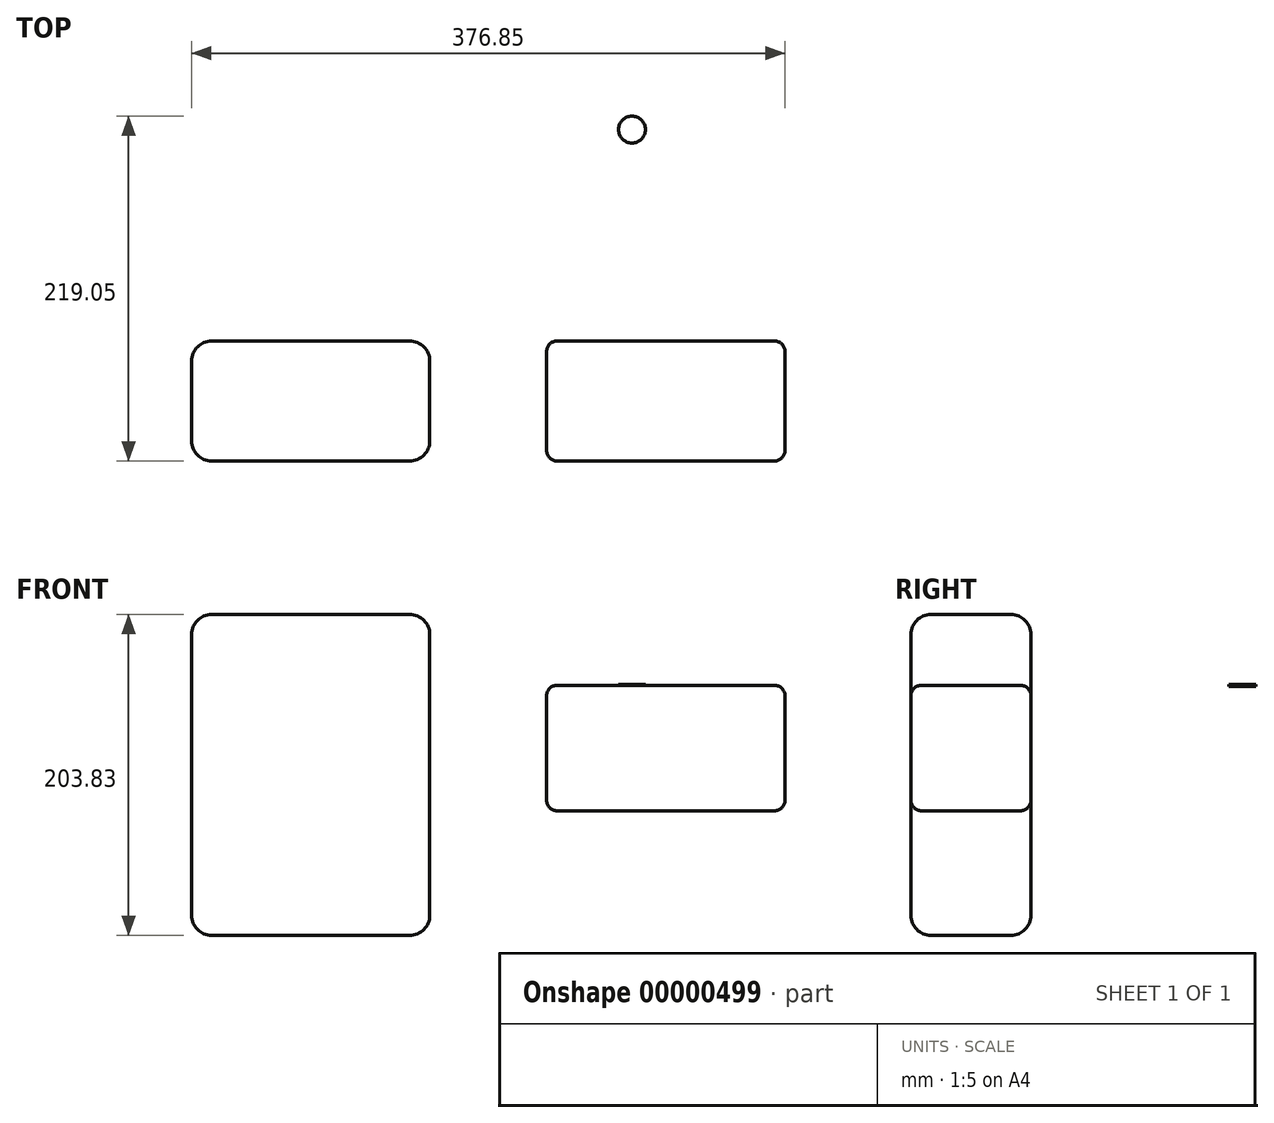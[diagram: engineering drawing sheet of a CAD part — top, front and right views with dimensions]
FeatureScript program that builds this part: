
annotation { "Feature Type Name" : "Feature", "Feature Type Description" : "" }
export const myFeature = defineFeature(function(context is Context, id is Id, definition is map)
    precondition{}
    {
        {
            var Q0;
            Q0=qCreatedBy(makeId("Front.planeOp"),FACE);
            var sketch = newSketch(context, id + "F0", { "sketchPlane" : qUnion([Q0])});
            skLineSegment(sketch, "E0.bottom", {"start": v(127.92, -65.75) * mm, "end": v(-23.48, -65.75) * mm});
            skLineSegment(sketch, "E0.top", {"start": v(127.92, 14) * mm, "end": v(-23.48, 14) * mm});
            skLineSegment(sketch, "E0.left", {"start": v(127.92, -65.75) * mm, "end": v(127.92, 14) * mm});
            skLineSegment(sketch, "E0.right", {"start": v(-23.48, -65.75) * mm, "end": v(-23.48, 14) * mm});
            skSolve(sketch);
        }
        {
            var Q0;
            Q0=makeQuery(id+"F0.imprint","IMPRINT",FACE,{"disambiguationData":[TD([[makeQuery(id+"F0.imprint","IMPRINT",EDGE,{"derivedFrom":sQuery(id+"F0.wireOp",EDGE,"E0.bottom")}),-1.0]])]});
            extrude(context, id + "F1", {"entities" : qUnion([Q0]), "depth" : 76.2 * mm});
        }
        {
            var Q0;
            Q0=qCreatedBy(makeId("Top.planeOp"),FACE);
            cPlane(context, id + "F2", {"entities" : qUnion([Q0]), "cplaneType" : CPlaneType.OFFSET, "offset" : 13.2 * mm, "width" : 152.4 * mm, "height" : 152.4 * mm});
        }
        {
            var Q0;
            Q0=qCreatedBy(id+"F2.planeOp",FACE);
            var sketch = newSketch(context, id + "F3", { "sketchPlane" : qUnion([Q0])});
            skCircle(sketch, "E1", {"center": v(30.72, 134.33) * mm, "radius": 8.53 * mm});
            skSolve(sketch);
        }
        {
            var Q0;
            Q0=makeQuery(id+"F3.imprint","IMPRINT",FACE,{"disambiguationData":[TD([[makeQuery(id+"F3.imprint","IMPRINT",EDGE,{"derivedFrom":sQuery(id+"F3.wireOp",EDGE,"E1")}),1.0]])]});
            extrude(context, id + "F4", {"entities" : qUnion([Q0]), "depth" : 1.27 * mm});
        }
        {
            var Q0;
            Q0=qCreatedBy(makeId("Front.planeOp"),FACE);
            var sketch = newSketch(context, id + "F5", { "sketchPlane" : qUnion([Q0])});
            skLineSegment(sketch, "E2.bottom", {"start": v(-97.7, 58.95) * mm, "end": v(-248.93, 58.95) * mm});
            skLineSegment(sketch, "E2.top", {"start": v(-97.7, -144.88) * mm, "end": v(-248.93, -144.88) * mm});
            skLineSegment(sketch, "E2.left", {"start": v(-97.7, 58.95) * mm, "end": v(-97.7, -144.88) * mm});
            skLineSegment(sketch, "E2.right", {"start": v(-248.93, 58.95) * mm, "end": v(-248.93, -144.88) * mm});
            skSolve(sketch);
        }
        {
            var Q0;
            Q0=makeQuery(id+"F5.imprint","IMPRINT",FACE,{"disambiguationData":[TD([[makeQuery(id+"F5.imprint","IMPRINT",EDGE,{"derivedFrom":sQuery(id+"F5.wireOp",EDGE,"E2.bottom")}),1.0]])]});
            extrude(context, id + "F6", {"entities" : qUnion([Q0]), "depth" : 76.2 * mm});
        }
        {
            var Q0;
            Q0=makeQuery(id+"F6.opExtrude","CAP_FACE",FACE,{"disambiguationData":[OSD([sQuery(id+"F5.wireOp",EDGE,"E2.bottom"),sQuery(id+"F5.wireOp",EDGE,"E2.top"),sQuery(id+"F5.wireOp",EDGE,"E2.left"),sQuery(id+"F5.wireOp",EDGE,"E2.right")])],"isStart":false});
            var Q1;
            Q1=makeQuery(id+"F6.opExtrude","SWEPT_FACE",FACE,{"disambiguationData":[OSD([sQuery(id+"F5.wireOp",EDGE,"E2.right")])]});
            var Q2;
            Q2=makeQuery(id+"F6.opExtrude","CAP_EDGE",EDGE,{"disambiguationData":[OSD([sQuery(id+"F5.wireOp",EDGE,"E2.bottom")])],"isStart":true});
            var Q3;
            Q3=makeQuery(id+"F6.opExtrude","SWEPT_FACE",FACE,{"disambiguationData":[OSD([sQuery(id+"F5.wireOp",EDGE,"E2.bottom")])]});
            var Q4;
            Q4=makeQuery(id+"F6.opExtrude","CAP_EDGE",EDGE,{"disambiguationData":[OSD([sQuery(id+"F5.wireOp",EDGE,"E2.left")])],"isStart":true});
            var Q5;
            Q5=makeQuery(id+"F6.opExtrude","CAP_FACE",FACE,{"disambiguationData":[OSD([sQuery(id+"F5.wireOp",EDGE,"E2.bottom"),sQuery(id+"F5.wireOp",EDGE,"E2.top"),sQuery(id+"F5.wireOp",EDGE,"E2.left"),sQuery(id+"F5.wireOp",EDGE,"E2.right")])],"isStart":true});
            var Q6;
            Q6=makeQuery(id+"F6.opExtrude","SWEPT_EDGE",EDGE,{"disambiguationData":[OSD([sQuery(id+"F5.wireOp",EDGE,"E2.top"),sQuery(id+"F5.wireOp",EDGE,"E2.left")])]});
            fillet(context, id + "F7", {"entities" : qUnion([Q0, Q1, Q2, Q3, Q4, Q5, Q6]), "radius" : 12.7 * mm, "tangentPropagation" : true, "allowEdgeOverflow" : false});
        }
        {
            var Q0;
            Q0=makeQuery(id+"F1.opExtrude","CAP_EDGE",EDGE,{"disambiguationData":[OSD([sQuery(id+"F0.wireOp",EDGE,"E0.right")])],"isStart":false});
            var Q1;
            Q1=makeQuery(id+"F1.opExtrude","CAP_EDGE",EDGE,{"disambiguationData":[OSD([sQuery(id+"F0.wireOp",EDGE,"E0.bottom")])],"isStart":false});
            var Q2;
            Q2=makeQuery(id+"F1.opExtrude","CAP_EDGE",EDGE,{"disambiguationData":[OSD([sQuery(id+"F0.wireOp",EDGE,"E0.left")])],"isStart":false});
            var Q3;
            Q3=makeQuery(id+"F1.opExtrude","SWEPT_EDGE",EDGE,{"disambiguationData":[OSD([sQuery(id+"F0.wireOp",EDGE,"E0.top"),sQuery(id+"F0.wireOp",EDGE,"E0.right")])]});
            var Q4;
            Q4=makeQuery(id+"F1.opExtrude","CAP_EDGE",EDGE,{"disambiguationData":[OSD([sQuery(id+"F0.wireOp",EDGE,"E0.top")])],"isStart":false});
            var Q5;
            Q5=makeQuery(id+"F1.opExtrude","SWEPT_EDGE",EDGE,{"disambiguationData":[OSD([sQuery(id+"F0.wireOp",EDGE,"E0.bottom"),sQuery(id+"F0.wireOp",EDGE,"E0.right")])]});
            var Q6;
            Q6=makeQuery(id+"F1.opExtrude","SWEPT_EDGE",EDGE,{"disambiguationData":[OSD([sQuery(id+"F0.wireOp",EDGE,"E0.bottom"),sQuery(id+"F0.wireOp",EDGE,"E0.left")])]});
            var Q7;
            Q7=makeQuery(id+"F1.opExtrude","SWEPT_EDGE",EDGE,{"disambiguationData":[OSD([sQuery(id+"F0.wireOp",EDGE,"E0.top"),sQuery(id+"F0.wireOp",EDGE,"E0.left")])]});
            var Q8;
            Q8=makeQuery(id+"F1.opExtrude","CAP_EDGE",EDGE,{"disambiguationData":[OSD([sQuery(id+"F0.wireOp",EDGE,"E0.bottom")])],"isStart":true});
            var Q9;
            Q9=makeQuery(id+"F1.opExtrude","CAP_EDGE",EDGE,{"disambiguationData":[OSD([sQuery(id+"F0.wireOp",EDGE,"E0.left")])],"isStart":true});
            var Q10;
            Q10=makeQuery(id+"F1.opExtrude","CAP_EDGE",EDGE,{"disambiguationData":[OSD([sQuery(id+"F0.wireOp",EDGE,"E0.top")])],"isStart":true});
            var Q11;
            Q11=makeQuery(id+"F1.opExtrude","CAP_EDGE",EDGE,{"disambiguationData":[OSD([sQuery(id+"F0.wireOp",EDGE,"E0.right")])],"isStart":true});
            fillet(context, id + "F8", {"entities" : qUnion([Q0, Q1, Q2, Q3, Q4, Q5, Q6, Q7, Q8, Q9, Q10, Q11]), "radius" : 6.6 * mm, "tangentPropagation" : true, "allowEdgeOverflow" : false});
        }
    });
